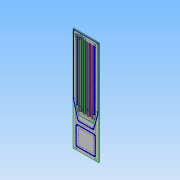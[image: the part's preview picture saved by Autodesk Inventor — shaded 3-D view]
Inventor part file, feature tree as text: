
AUTODESK INVENTOR PART (.ipt)
format: ipt  version: 2013 (Build 170138000, 138)  size: 377,344 bytes
history: native  units: in
note: dims shown in document units (in); Inventor stores cm internally (conversion verified against a paired STEP export)
features: other x13, extrude x3, hole x1, plane x1, sketch x1
ambient origin geometry x8: Origin, YZ Plane, XZ Plane, XY Plane, X Axis, Y Axis, Z Axis, Center Point
bodies: Solid1 (feature_tree)
feature tree (19):
  other  "Blocks"
  extrude  "Stock Extrusion"  Depth=96.0in
  extrude  "Main rope pocket"  TaperAngle=0.0deg  [1 undecoded]
  other  "Side profile reference"
  hole  "Hole1"  [1 undecoded]
  plane  "Work Plane1"
  extrude  "Through Panel Extrusion5"  Depth=1.0in
  other  "Exclaim Point"
  sketch  "Sketch11"  dims[d1=23.8125in d2=96.0in d3=0.0in d4=58.0in d6=1.0in d7=2.9062in d9=0.24in d10=0.24in d18=2.5in d19=4.75in d20=96.0in d21=21.3125in d22=58.0in d23=2.0in d25=0.24in d26=0.24in d29=2.0in d32=2.5in d33=1.74in d38=33.25in d41=58.0in d42=2.0in d43=0.24in d44=0.24in d45=2.0in d47=2.0in d49=58.0in d50=2.0in d51=1.0in d52=0.24in d53=0.24in d73=0.55in d74=0.47in d75=0.5in d76=0.58in d80=0.48in d88=0.25in d89=4.75in d90=2.5in d91=0.75in d92=1.0in d93=0.1in d94=0.25in d95=0.5in d96=0.25in d97=0.205in d98=0.0in d99=0.5in d100=0.75in d102=1.375in d105=0.3125in d109=1.3in d110=1.375in d111=1.375in d112=0.75in d113=2.125in d114=2.125in d115=1.375in d116=1.375in d117=0.75in d119=0.3125in d120=0.75in d121=0.75in d122=0.25in d123=0.5635in d124=1.0in d125=0.8108in d126=2.875in d127=1.75in d129=2.25in d130=0.1875in d131=4.0in d132=0.0in d133=0.0in d138=2.5in d139=0.41in d140=0.41in d141=0.41in d142=165.0deg d144=2.5in d145=2.5in d146=2.5in d147=2.5in d148=0.66in d149=0.66in d150=0.66in d151=3.5in d152=16.0in d154=0.75in d155=0.75in d156=0.16in d157=0.32in d158=0.75in d159=0.16in d160=0.32in d161=2.5in d162=1.25in d163=2.5in d164=8.0in d165=2.5in d166=14.5in d167=0.48in d168=1.0in d169=0.5in d170=0.0in d171=0.48in d172=165.0deg d173=0.5in d174=2.7559in d176=2.0in d177=0.3937in d179=1.0in d181=0.5in d182=0.7874in d184=16.0in d185=0.3937in d187=1.0in]
  other  "Stock"
  other  "LEDPocket"
  other  "TwoLineColumn"
  other  "TwoLineColumnEnd"
  other  "15mm Neon profile"
  other  "U Bolt hole and bore"
  other  "U-Bolt holes"
  other  "WeatherProof panel"
  other  "15mm Neon profile:1"
  other  "15mm Neon profile:2"
note: 2 required parameter values undecoded (feature->parameter linkage not recoverable at this tier; creation-order binding heuristic only, values carry confidence <= 0.55)
